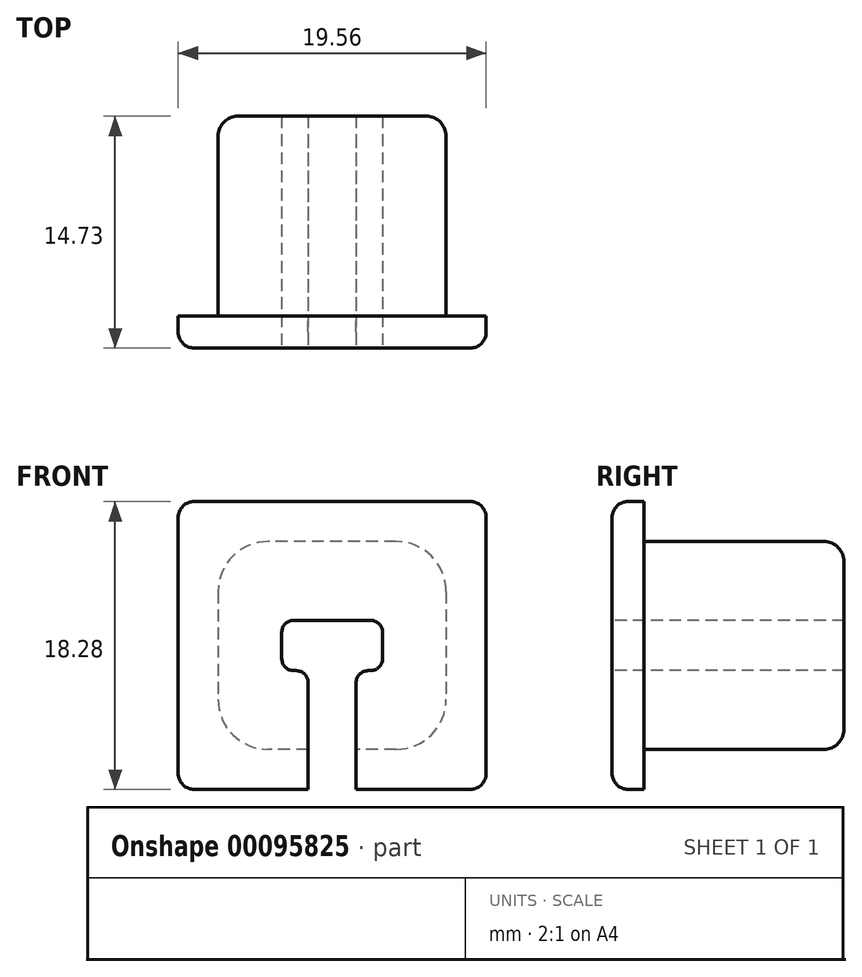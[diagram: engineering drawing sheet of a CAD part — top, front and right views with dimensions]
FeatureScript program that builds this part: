
annotation { "Feature Type Name" : "Feature", "Feature Type Description" : "" }
export const myFeature = defineFeature(function(context is Context, id is Id, definition is map)
    precondition{}
    {
        {
            var Q0;
            Q0=qCreatedBy(makeId("Front.planeOp"),FACE);
            var sketch = newSketch(context, id + "F0", { "sketchPlane" : qUnion([Q0])});
            skLineSegment(sketch, "E0.bottom", {"start": v(7.24, 6.6) * mm, "end": v(-7.24, 6.6) * mm});
            skLineSegment(sketch, "E0.top", {"start": v(7.24, -6.6) * mm, "end": v(-7.24, -6.6) * mm});
            skLineSegment(sketch, "E0.left", {"start": v(7.24, 6.6) * mm, "end": v(7.24, -6.6) * mm});
            skLineSegment(sketch, "E0.right", {"start": v(-7.24, 6.6) * mm, "end": v(-7.24, -6.6) * mm});
            skPoint(sketch, "E0.middle", {"position": v(0, 0) * mm});
            skLineSegment(sketch, "E1.0", {"start": v(9.78, 9.14) * mm, "end": v(-9.78, 9.14) * mm});
            skLineSegment(sketch, "E1.1", {"start": v(9.78, 9.14) * mm, "end": v(9.78, -9.14) * mm});
            skLineSegment(sketch, "E1.2", {"start": v(9.78, -9.14) * mm, "end": v(-9.78, -9.14) * mm});
            skLineSegment(sketch, "E1.3", {"start": v(-9.78, 9.14) * mm, "end": v(-9.78, -9.14) * mm});
            skSolve(sketch);
        }
        {
            var Q0;
            Q0=makeQuery(id+"F0.imprint","IMPRINT",FACE,{"disambiguationData":[TD([[makeQuery(id+"F0.imprint","IMPRINT",EDGE,{"derivedFrom":sQuery(id+"F0.wireOp",EDGE,"E0.bottom")}),1.0]])]});
            extrude(context, id + "F1", {"entities" : qUnion([Q0]), "oppositeDirection" : true, "depth" : 12.7 * mm});
        }
        {
            var Q0;
            Q0=makeQuery(id+"F1.opExtrude","SWEPT_EDGE",EDGE,{"disambiguationData":[OSD([sQuery(id+"F0.wireOp",EDGE,"E0.bottom"),sQuery(id+"F0.wireOp",EDGE,"E0.right")])]});
            var Q1;
            Q1=makeQuery(id+"F1.opExtrude","SWEPT_EDGE",EDGE,{"disambiguationData":[OSD([sQuery(id+"F0.wireOp",EDGE,"E0.bottom"),sQuery(id+"F0.wireOp",EDGE,"E0.left")])]});
            var Q2;
            Q2=makeQuery(id+"F1.opExtrude","SWEPT_EDGE",EDGE,{"disambiguationData":[OSD([sQuery(id+"F0.wireOp",EDGE,"E0.top"),sQuery(id+"F0.wireOp",EDGE,"E0.left")])]});
            var Q3;
            Q3=makeQuery(id+"F1.opExtrude","SWEPT_EDGE",EDGE,{"disambiguationData":[OSD([sQuery(id+"F0.wireOp",EDGE,"E0.top"),sQuery(id+"F0.wireOp",EDGE,"E0.right")])]});
            fillet(context, id + "F2", {"entities" : qUnion([Q0, Q1, Q2, Q3]), "radius" : 3.17 * mm, "tangentPropagation" : true, "allowEdgeOverflow" : false});
        }
        {
            var Q0;
            Q0=makeQuery(id+"F0.imprint","IMPRINT",FACE,{"disambiguationData":[TD([[makeQuery(id+"F0.imprint","IMPRINT",EDGE,{"derivedFrom":sQuery(id+"F0.wireOp",EDGE,"E0.bottom")}),-1.0]])]});
            var Q1;
            Q1=makeQuery(id+"F0.imprint","IMPRINT",FACE,{"disambiguationData":[TD([[makeQuery(id+"F0.imprint","IMPRINT",EDGE,{"derivedFrom":sQuery(id+"F0.wireOp",EDGE,"E0.bottom")}),1.0]])]});
            extrude(context, id + "F3", {"entities" : qUnion([Q0, Q1]), "operationType" : NewBodyOperationType.ADD, "depth" : 2.03 * mm});
        }
        {
            var Q0;
            Q0=makeQuery(id+"F3.opExtrude","CAP_FACE",FACE,{"disambiguationData":[OSD([sQuery(id+"F0.wireOp",EDGE,"E1.0"),sQuery(id+"F0.wireOp",EDGE,"E1.1"),sQuery(id+"F0.wireOp",EDGE,"E1.2"),sQuery(id+"F0.wireOp",EDGE,"E1.3")])],"isStart":false});
            var sketch = newSketch(context, id + "F4", { "sketchPlane" : qUnion([Q0])});
            skLineSegment(sketch, "E2.bottom", {"start": v(1.52, 0) * mm, "end": v(-1.52, 0) * mm});
            skLineSegment(sketch, "E2.top", {"start": v(1.52, -18.29) * mm, "end": v(-1.52, -18.29) * mm});
            skLineSegment(sketch, "E2.left", {"start": v(1.52, 0) * mm, "end": v(1.52, -18.29) * mm});
            skLineSegment(sketch, "E2.right", {"start": v(-1.52, 0) * mm, "end": v(-1.52, -18.29) * mm});
            skPoint(sketch, "E2.middle", {"position": v(0, -9.14) * mm});
            skLineSegment(sketch, "E3.bottom", {"start": v(3.2, -1.6) * mm, "end": v(-3.2, -1.6) * mm});
            skLineSegment(sketch, "E3.top", {"start": v(3.2, 1.6) * mm, "end": v(-3.2, 1.6) * mm});
            skLineSegment(sketch, "E3.left", {"start": v(3.2, -1.6) * mm, "end": v(3.2, 1.6) * mm});
            skLineSegment(sketch, "E3.right", {"start": v(-3.2, -1.6) * mm, "end": v(-3.2, 1.6) * mm});
            skPoint(sketch, "E3.middle", {"position": v(0, 0) * mm});
            skSolve(sketch);
        }
        {
            var Q0;
            Q0=makeQuery(id+"F3.opExtrude","SWEPT_EDGE",EDGE,{"disambiguationData":[OSD([sQuery(id+"F0.wireOp",EDGE,"E1.0"),sQuery(id+"F0.wireOp",EDGE,"E1.1")])]});
            var Q1;
            Q1=makeQuery(id+"F3.opExtrude","SWEPT_EDGE",EDGE,{"disambiguationData":[OSD([sQuery(id+"F0.wireOp",EDGE,"E1.0"),sQuery(id+"F0.wireOp",EDGE,"E1.3")])]});
            var Q2;
            Q2=makeQuery(id+"F3.opExtrude","SWEPT_EDGE",EDGE,{"disambiguationData":[OSD([sQuery(id+"F0.wireOp",EDGE,"E1.2"),sQuery(id+"F0.wireOp",EDGE,"E1.3")])]});
            var Q3;
            Q3=makeQuery(id+"F3.opExtrude","SWEPT_EDGE",EDGE,{"disambiguationData":[OSD([sQuery(id+"F0.wireOp",EDGE,"E1.1"),sQuery(id+"F0.wireOp",EDGE,"E1.2")])]});
            var Q4;
            Q4=makeQuery(id+"F3.opExtrude","CAP_EDGE",EDGE,{"disambiguationData":[OSD([sQuery(id+"F0.wireOp",EDGE,"E1.0")])],"isStart":false});
            var Q5;
            Q5=makeQuery(id+"F3.opExtrude","CAP_EDGE",EDGE,{"disambiguationData":[OSD([sQuery(id+"F0.wireOp",EDGE,"E1.1")])],"isStart":false});
            var Q6;
            Q6=makeQuery(id+"F3.opExtrude","CAP_EDGE",EDGE,{"disambiguationData":[OSD([sQuery(id+"F0.wireOp",EDGE,"E1.3")])],"isStart":false});
            var Q7;
            Q7=makeQuery(id+"F3.opExtrude","CAP_EDGE",EDGE,{"disambiguationData":[OSD([sQuery(id+"F0.wireOp",EDGE,"E1.2")])],"isStart":false});
            fillet(context, id + "F5", {"entities" : qUnion([Q0, Q1, Q2, Q3, Q4, Q5, Q6, Q7]), "radius" : 1.02 * mm, "tangentPropagation" : true, "allowEdgeOverflow" : false});
        }
        {
            var Q0;
            Q0 = qSketchRegion(id + "F4", true);
            extrude(context, id + "F6", {"entities" : qUnion([Q0]), "operationType" : NewBodyOperationType.REMOVE, "endBound" : BoundingType.THROUGH_ALL, "oppositeDirection" : true, "depth" : 15.24 * mm});
        }
        {
            var Q0;
            Q0=makeQuery(id+"F6.boolean.opBoolean","COPY",EDGE,{"derivedFrom":makeQuery(id+"F6.opExtrude","CAP_EDGE",EDGE,{"disambiguationData":[OSD([sQuery(id+"F4.wireOp",EDGE,"0l6Fcy6Q-fmhL-8gER-ke7l-APjaoghuo2Ds")])],"isStart":true})});
            var Q1;
            Q1=makeQuery(id+"F6.boolean.opBoolean","COPY",EDGE,{"derivedFrom":makeQuery(id+"F6.opExtrude","CAP_EDGE",EDGE,{"disambiguationData":[OSD([sQuery(id+"F4.wireOp",EDGE,"E2.right")])],"isStart":true})});
            var Q2;
            Q2=makeQuery(id+"F6.boolean.opBoolean","COPY",EDGE,{"derivedFrom":makeQuery(id+"F6.opExtrude","CAP_EDGE",EDGE,{"disambiguationData":[OSD([sQuery(id+"F4.wireOp",EDGE,"E2.left")])],"isStart":true})});
            var Q3;
            Q3=makeQuery(id+"F6.boolean.opBoolean","COPY",EDGE,{"derivedFrom":makeQuery(id+"F6.opExtrude","SWEPT_EDGE",EDGE,{"disambiguationData":[OSD([sQuery(id+"F4.wireOp",EDGE,"0l6Fcy6Q-fmhL-8gER-ke7l-APjaoghuo2Ds"),sQuery(id+"F4.wireOp",EDGE,"E2.right")])]})});
            var Q4;
            Q4=makeQuery(id+"F6.boolean.opBoolean","COPY",EDGE,{"derivedFrom":makeQuery(id+"F6.opExtrude","SWEPT_EDGE",EDGE,{"disambiguationData":[OSD([sQuery(id+"F4.wireOp",EDGE,"0l6Fcy6Q-fmhL-8gER-ke7l-APjaoghuo2Ds"),sQuery(id+"F4.wireOp",EDGE,"E2.left")])]})});
            var Q5;
            Q5=makeQuery(id+"F6.boolean.opBoolean","INTERSECT",EDGE,{"derivedFrom":[makeQuery(id+"F1.opExtrude","CAP_FACE",FACE,{"disambiguationData":[OSD([sQuery(id+"F0.wireOp",EDGE,"E0.bottom"),sQuery(id+"F0.wireOp",EDGE,"E0.top"),sQuery(id+"F0.wireOp",EDGE,"E0.left"),sQuery(id+"F0.wireOp",EDGE,"E0.right")])],"isStart":false}),makeQuery(id+"F6.opExtrude","SWEPT_FACE",FACE,{"disambiguationData":[OSD([sQuery(id+"F4.wireOp",EDGE,"0l6Fcy6Q-fmhL-8gER-ke7l-APjaoghuo2Ds")])]})]});
            var Q6;
            Q6=makeQuery(id+"F6.boolean.opBoolean","COPY",EDGE,{"derivedFrom":makeQuery(id+"F6.opExtrude","SWEPT_EDGE",EDGE,{"disambiguationData":[OSD([sQuery(id+"F4.wireOp",EDGE,"E3.bottom"),sQuery(id+"F4.wireOp",EDGE,"E3.right")])]})});
            var Q7;
            Q7=makeQuery(id+"F6.boolean.opBoolean","COPY",EDGE,{"derivedFrom":makeQuery(id+"F6.opExtrude","SWEPT_EDGE",EDGE,{"disambiguationData":[OSD([sQuery(id+"F4.wireOp",EDGE,"E3.bottom"),sQuery(id+"F4.wireOp",EDGE,"E3.left")])]})});
            var Q8;
            Q8=makeQuery(id+"F6.boolean.opBoolean","COPY",EDGE,{"derivedFrom":makeQuery(id+"F6.opExtrude","SWEPT_EDGE",EDGE,{"disambiguationData":[OSD([sQuery(id+"F4.wireOp",EDGE,"E3.top"),sQuery(id+"F4.wireOp",EDGE,"E3.left")])]})});
            var Q9;
            Q9=makeQuery(id+"F6.boolean.opBoolean","COPY",EDGE,{"derivedFrom":makeQuery(id+"F6.opExtrude","SWEPT_EDGE",EDGE,{"disambiguationData":[OSD([sQuery(id+"F4.wireOp",EDGE,"E3.top"),sQuery(id+"F4.wireOp",EDGE,"E3.right")])]})});
            var Q10;
            {var subQ0=sQuery(id+"F4.wireOp",EDGE,"E3.bottom");Q10=makeQuery(id+"F6.boolean.opBoolean","COPY",EDGE,{"derivedFrom":makeQuery(id+"F6.opExtrude","CAP_EDGE",EDGE,{"disambiguationData":[OSD([subQ0]),TDD([makeQuery(id+"F4.imprint","IMPRINT",EDGE,{"disambiguationData":[TD([[makeQuery(id+"F4.imprint","INTERSECT",VERTEX,{"derivedFrom":[subQ0,sQuery(id+"F4.wireOp",EDGE,"E3.right")]}),1.0]])],"derivedFrom":subQ0})])],"isStart":true})});}
            var Q11;
            {var subQ0=sQuery(id+"F4.wireOp",EDGE,"E3.bottom");Q11=makeQuery(id+"F6.boolean.opBoolean","COPY",EDGE,{"derivedFrom":makeQuery(id+"F6.opExtrude","CAP_EDGE",EDGE,{"disambiguationData":[OSD([subQ0]),TDD([makeQuery(id+"F4.imprint","IMPRINT",EDGE,{"disambiguationData":[TD([[makeQuery(id+"F4.imprint","INTERSECT",VERTEX,{"derivedFrom":[subQ0,sQuery(id+"F4.wireOp",EDGE,"E3.left")]}),-1.0]])],"derivedFrom":subQ0})])],"isStart":true})});}
            fillet(context, id + "F7", {"entities" : qUnion([Q0, Q1, Q2, Q3, Q4, Q5, Q6, Q7, Q8, Q9, Q10, Q11]), "radius" : 0.76 * mm, "tangentPropagation" : true, "allowEdgeOverflow" : false});
        }
        {
            var Q0;
            Q0=makeQuery(id+"F1.opExtrude","CAP_EDGE",EDGE,{"disambiguationData":[OSD([sQuery(id+"F0.wireOp",EDGE,"E0.right")])],"isStart":false});
            var Q1;
            Q1=makeQuery(id+"F1.opExtrude","CAP_EDGE",EDGE,{"disambiguationData":[OSD([sQuery(id+"F0.wireOp",EDGE,"E0.bottom")])],"isStart":false});
            var Q2;
            Q2=makeQuery(id+"F1.opExtrude","CAP_EDGE",EDGE,{"disambiguationData":[OSD([sQuery(id+"F0.wireOp",EDGE,"E0.left")])],"isStart":false});
            var Q3;
            {var subQ1=sQuery(id+"F0.wireOp",EDGE,"E0.top");Q3=makeQuery(id+"F6.boolean.opBoolean","SPLIT",EDGE,{"disambiguationData":[TD([makeQuery(id+"F6.opExtrude","SWEPT_FACE",FACE,{"disambiguationData":[OSD([sQuery(id+"F4.wireOp",EDGE,"E2.left")])]})])],"derivedFrom":makeQuery(id+"F1.opExtrude","CAP_EDGE",EDGE,{"disambiguationData":[OSD([subQ1])],"isStart":false})});}
            var Q4;
            {var subQ1=sQuery(id+"F0.wireOp",EDGE,"E0.top");Q4=makeQuery(id+"F6.boolean.opBoolean","SPLIT",EDGE,{"disambiguationData":[TD([makeQuery(id+"F6.opExtrude","SWEPT_FACE",FACE,{"disambiguationData":[OSD([sQuery(id+"F4.wireOp",EDGE,"E2.right")])]})])],"derivedFrom":makeQuery(id+"F1.opExtrude","CAP_EDGE",EDGE,{"disambiguationData":[OSD([subQ1])],"isStart":false})});}
            fillet(context, id + "F8", {"entities" : qUnion([Q0, Q1, Q2, Q3, Q4]), "radius" : 1.27 * mm, "tangentPropagation" : true, "allowEdgeOverflow" : false});
        }
    });
